# Revit family: LEGRAND_PRISES_NON_VERROUILLEES_ENCASTREES_IP44_440
name_source: partatom
category: Installations électriques
revit_build: Autodesk Revit 2018 (Build: 20170223_1515(x64)
units: mm (PartAtom-declared; Revit-internal decimal feet)

## family parameters
Conserver l'orientation des annotations = Non
Cote de connecteur circulaire = Utiliser le diamètre
Couper avec des vides une fois chargée = Non
Hôte = Face
Partagée = Non
Point de calcul de pièce = Non
Type d'élément = Normal

## types (3) — shared parameters
Conditions Générale d'Utilisation = https://export.legrand.com
Couleur caractéristique = rouge
Description = Prise au standard international pour montage encastré ou saillie avec accessoire permet la connexion d'appareils de puissance
Elévation par défaut = 1000 mm  [stored 3.28084 ft]
Fabricant = Legrand
Nombre de pôles = 4
Standard CEI ou NFC = CEI
Température maximale d'installation = 40°C
Température maximum d'utilisation = 100°C
Température minimum d'installation = -20°C
Température minimum d'utilisation = -50°C
Tension V = 400 440 V  50 60 Hz  rouge
entraxe de fixation vertical mm = 70 mm
installation Encastrée E ou Saillie S = encastré et saillie
matériau du boitier = plastique
résistance aux chocs IK = 09
type de raccordement = bornes à vis

## per-type parameters (varying)
| type | Dia bouchon | Intensité A | Modèle | Position de la Terre h | RAY BOUCHON | Ray | classe de protection IP | entraxe de fixation horizontal mm | h1 | hauteur mm | largeur mm | profondeur d'encastrement mm | profondeur mm | sans halogène |
| Socle tableau Hypra   IP44   TBT 16 A   440/460 V   2P+T   plast | 48 mm | 16 A | 052310 | 11 | 24 mm | 24 mm | IP44 | 60 mm | 50 mm | 84 mm | 74 mm | 44 mm | 84 mm | Oui |
| Socle tableau à entraxe unifié Hypra   IP44   32 A   440/460V   3P+T   plast | 55 mm | 32 A | 052350 | 11 | 27 mm | 27 mm | IP44 | 70 mm | 56 mm | 94 mm | 84 mm | 50 mm | 99 mm | Oui |
| Socle tableau entraxe unifié Hypra IP66/67-55 32A 440V conteneur frigo 3P+T plast | 55 mm | 32 A | 052926 | 3 | 27 mm | 27 mm | IP66/67-55 | 70 mm | 56 mm | 94 mm | 84 mm | 54 mm | 104 mm | Non |

note: [stored X ft] marks values corroborated as IEEE doubles in the binary element streams (Revit-internal decimal feet)
